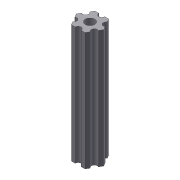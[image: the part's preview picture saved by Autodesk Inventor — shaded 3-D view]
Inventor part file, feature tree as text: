
AUTODESK INVENTOR PART (.ipt)
format: ipt  version: 2012 (Build 160160000, 160)  size: 94,720 bytes
history: native  units: in
note: dims shown in document units (in); Inventor stores cm internally (conversion verified against a paired STEP export)
features: extrude x2, sketch x2, pattern_circular x1
ambient origin geometry x8: Origin, YZ Plane, XZ Plane, XY Plane, X Axis, Y Axis, Z Axis, Center Point
bodies: Solid1 (feature_tree)
feature tree (5):
  extrude  "Extrusion1"  Depth=0.2in
  extrude  "Extrusion2"  Depth=0.0625in
  pattern_circular  "Circular Pattern1"  [2 undecoded]
  sketch  "Sketch1"  dims[d0=0.5in d1=0.2in]
  sketch  "Sketch2"  dims[d2=2.5in d3=0.0in d4=0.0625in d5=3.0in d6=0.0in d7=2.3622in d8=360.0deg]
note: 2 required parameter values undecoded (feature->parameter linkage not recoverable at this tier; creation-order binding heuristic only, values carry confidence <= 0.55)
